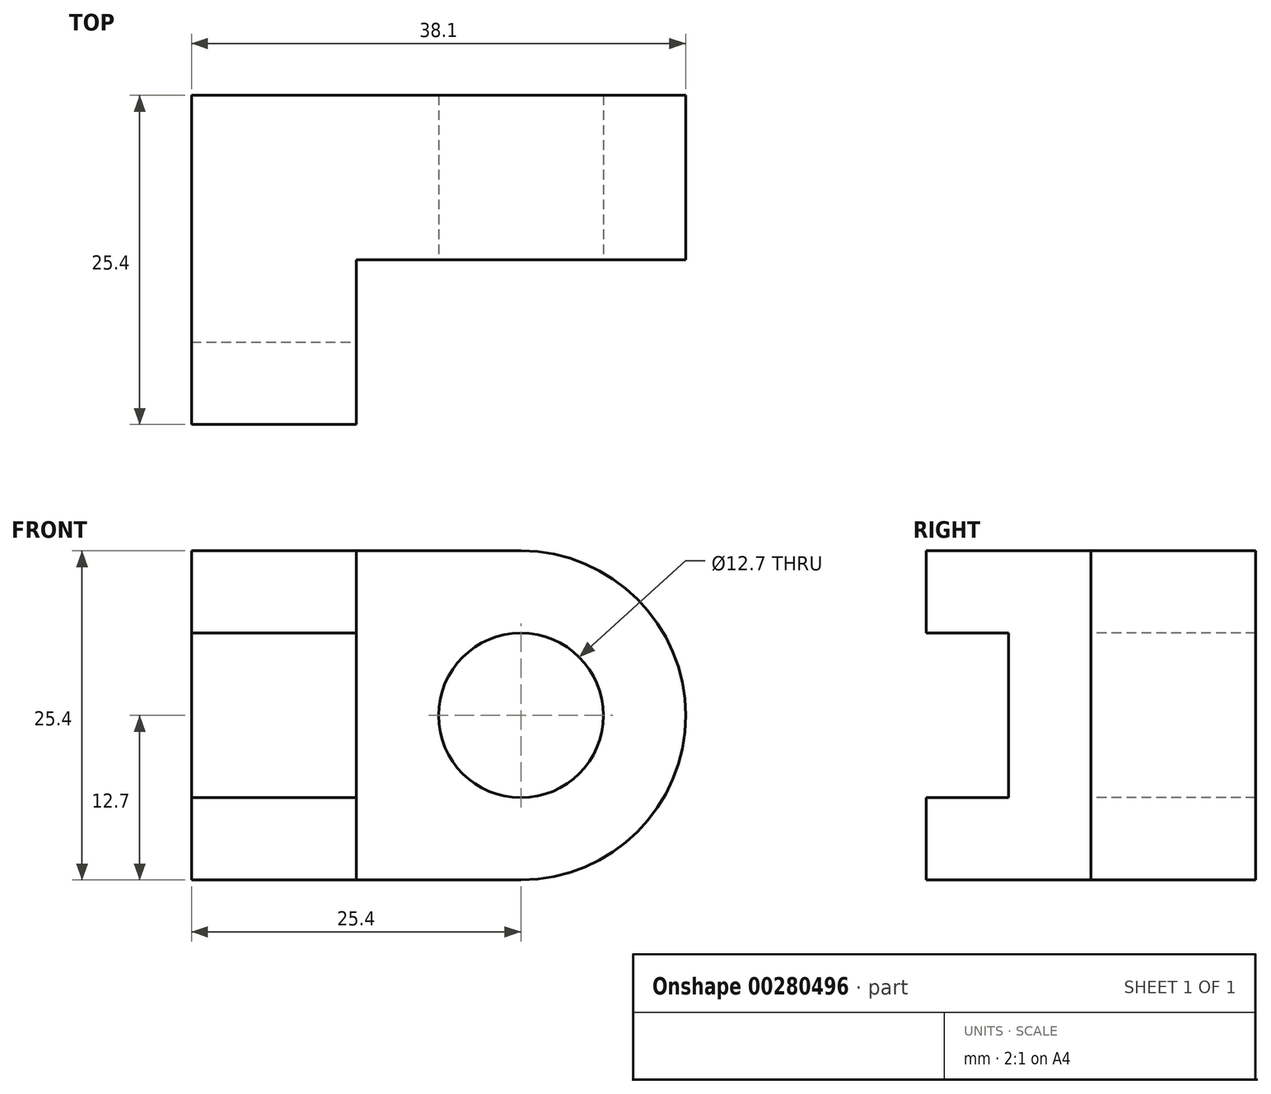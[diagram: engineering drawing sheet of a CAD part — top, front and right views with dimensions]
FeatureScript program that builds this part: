
annotation { "Feature Type Name" : "Feature", "Feature Type Description" : "" }
export const myFeature = defineFeature(function(context is Context, id is Id, definition is map)
    precondition{}
    {
        {
            var Q0;
            Q0=qCreatedBy(makeId("Front.planeOp"),FACE);
            var sketch = newSketch(context, id + "F0", { "sketchPlane" : qUnion([Q0])});
            skLineSegment(sketch, "E0", {"start": v(0, 0) * mm, "end": v(0, 25.4) * mm});
            skLineSegment(sketch, "E1", {"start": v(0, 25.4) * mm, "end": v(12.7, 25.4) * mm});
            skLineSegment(sketch, "E2", {"start": v(0, 0) * mm, "end": v(-12.7, 0) * mm});
            skLineSegment(sketch, "E3", {"start": v(-12.7, 0) * mm, "end": v(-12.7, 6.35) * mm});
            skLineSegment(sketch, "E4", {"start": v(-12.7, 6.35) * mm, "end": v(0, 6.35) * mm});
            skLineSegment(sketch, "E5", {"start": v(-12.7, 6.35) * mm, "end": v(-12.7, 19.05) * mm});
            skLineSegment(sketch, "E6", {"start": v(-12.7, 19.05) * mm, "end": v(-12.7, 25.4) * mm});
            skLineSegment(sketch, "E7", {"start": v(-12.7, 25.4) * mm, "end": v(0, 25.4) * mm});
            skLineSegment(sketch, "E8", {"start": v(-12.7, 19.05) * mm, "end": v(0, 19.05) * mm});
            skLineSegment(sketch, "E9", {"start": v(0, 0) * mm, "end": v(12.7, 0) * mm});
            skArc(sketch, "E10", {"start": v(12.7, 25.4) * mm, "mid": v(25.4, 12.7) * mm, "end": v(12.7, 0) * mm});
            skCircle(sketch, "E11", {"center": v(12.7, 12.7) * mm, "radius": 6.35 * mm});
            skSolve(sketch);
        }
        {
            var Q0;
            Q0=makeQuery(id+"F0.imprint","IMPRINT",FACE,{"disambiguationData":[TD([[makeQuery(id+"F0.imprint","IMPRINT",EDGE,{"derivedFrom":sQuery(id+"F0.wireOp",EDGE,"E6")}),-1.0]])]});
            var Q1;
            {var subQ0=sQuery(id+"F0.wireOp",EDGE,"E4");Q1=makeQuery(id+"F0.imprint","IMPRINT",FACE,{"disambiguationData":[TD([[makeQuery(id+"F0.imprint","IMPRINT",EDGE,{"derivedFrom":subQ0}),1.0]])]});}
            var Q2;
            {var subQ0=sQuery(id+"F0.wireOp",EDGE,"E2");Q2=makeQuery(id+"F0.imprint","IMPRINT",FACE,{"disambiguationData":[TD([[makeQuery(id+"F0.imprint","IMPRINT",EDGE,{"derivedFrom":subQ0}),-1.0]])]});}
            var Q3;
            {var subQ0=sQuery(id+"F0.wireOp",EDGE,"E1");Q3=makeQuery(id+"F0.imprint","IMPRINT",FACE,{"disambiguationData":[TD([[makeQuery(id+"F0.imprint","IMPRINT",EDGE,{"derivedFrom":subQ0}),-1.0]])]});}
            extrude(context, id + "F1", {"entities" : qUnion([Q0, Q1, Q2, Q3]), "oppositeDirection" : true, "depth" : 12.7 * mm});
        }
        {
            var Q0;
            {var subQ0=sQuery(id+"F0.wireOp",EDGE,"E2");Q0=makeQuery(id+"F0.imprint","IMPRINT",FACE,{"disambiguationData":[TD([[makeQuery(id+"F0.imprint","IMPRINT",EDGE,{"derivedFrom":subQ0}),-1.0]])]});}
            var Q1;
            Q1=makeQuery(id+"F0.imprint","IMPRINT",FACE,{"disambiguationData":[TD([[makeQuery(id+"F0.imprint","IMPRINT",EDGE,{"derivedFrom":sQuery(id+"F0.wireOp",EDGE,"E6")}),-1.0]])]});
            extrude(context, id + "F2", {"entities" : qUnion([Q0, Q1]), "operationType" : NewBodyOperationType.ADD, "depth" : 12.7 * mm});
        }
        {
            var Q0;
            {var subQ0=sQuery(id+"F0.wireOp",EDGE,"E4");Q0=makeQuery(id+"F0.imprint","IMPRINT",FACE,{"disambiguationData":[TD([[makeQuery(id+"F0.imprint","IMPRINT",EDGE,{"derivedFrom":subQ0}),1.0]])]});}
            extrude(context, id + "F3", {"entities" : qUnion([Q0]), "operationType" : NewBodyOperationType.ADD, "depth" : 6.35 * mm});
        }
    });
